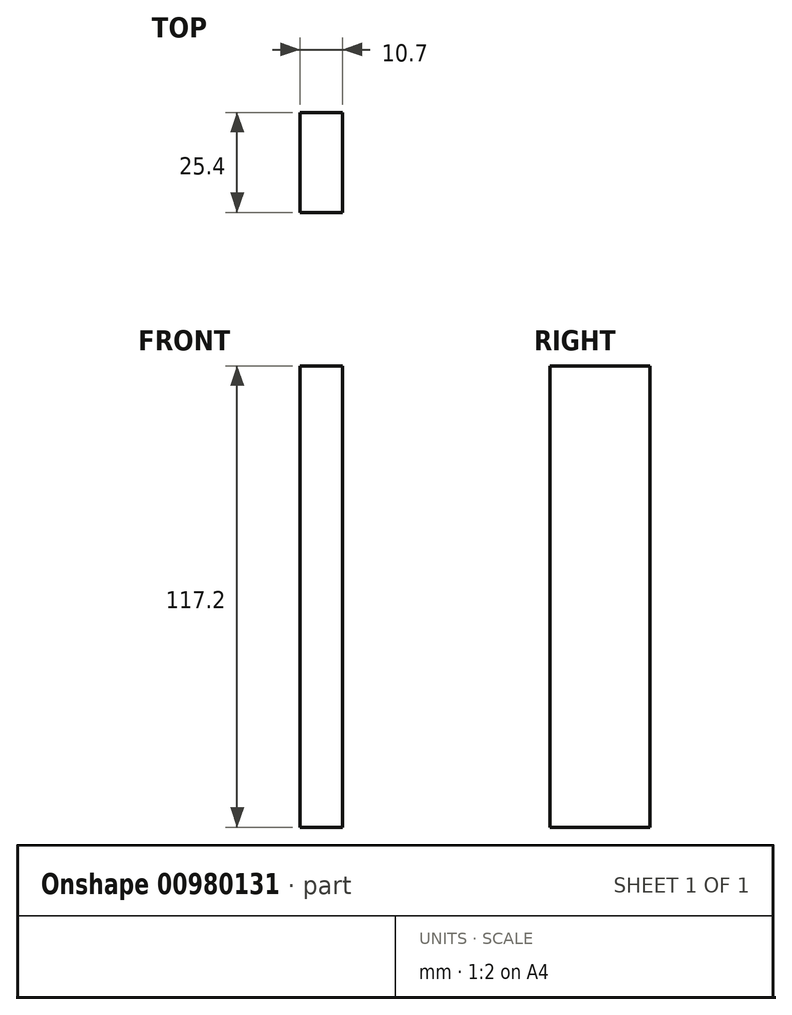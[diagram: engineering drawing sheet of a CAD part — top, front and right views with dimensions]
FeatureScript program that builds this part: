
annotation { "Feature Type Name" : "Feature", "Feature Type Description" : "" }
export const myFeature = defineFeature(function(context is Context, id is Id, definition is map)
    precondition{}
    {
        {
            var Q0;
            Q0=qCreatedBy(makeId("Front.planeOp"),FACE);
            var sketch = newSketch(context, id + "F0", { "sketchPlane" : qUnion([Q0])});
            skLineSegment(sketch, "E0.bottom", {"start": v(-59.54, 58.2) * mm, "end": v(-48.84, 58.2) * mm});
            skLineSegment(sketch, "E0.top", {"start": v(-59.54, -59) * mm, "end": v(-48.84, -59) * mm});
            skLineSegment(sketch, "E0.left", {"start": v(-59.54, 58.2) * mm, "end": v(-59.54, -59) * mm});
            skLineSegment(sketch, "E0.right", {"start": v(-48.84, 58.2) * mm, "end": v(-48.84, -59) * mm});
            skSolve(sketch);
        }
        {
            var Q0;
            Q0=makeQuery(id+"F0.imprint","IMPRINT",FACE,{"disambiguationData":[TD([[makeQuery(id+"F0.imprint","IMPRINT",EDGE,{"derivedFrom":sQuery(id+"F0.wireOp",EDGE,"E0.bottom")}),-1.0]])]});
            extrude(context, id + "F1", {"entities" : qUnion([Q0]), "endBound" : BoundingType.SYMMETRIC, "depth" : 25.4 * mm, "offsetDistance" : 25.4 * mm});
        }
    });
